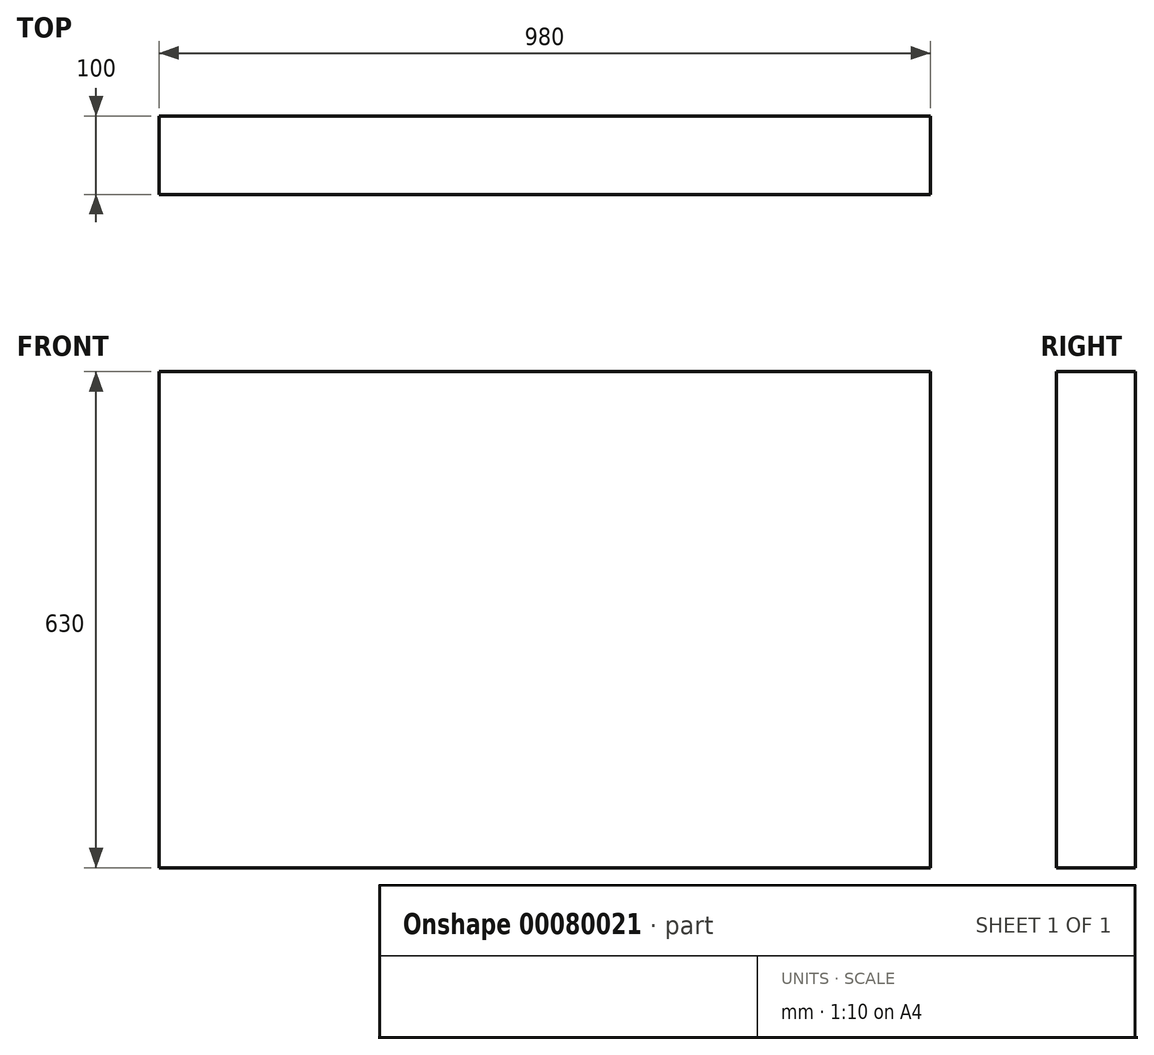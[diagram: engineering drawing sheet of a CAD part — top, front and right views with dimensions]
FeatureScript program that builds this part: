
annotation { "Feature Type Name" : "Feature", "Feature Type Description" : "" }
export const myFeature = defineFeature(function(context is Context, id is Id, definition is map)
    precondition{}
    {
        {
            var Q0;
            Q0=qCreatedBy(makeId("Front.planeOp"),FACE);
            var sketch = newSketch(context, id + "F0", { "sketchPlane" : qUnion([Q0])});
            skLineSegment(sketch, "E0.bottom", {"start": v(0, 0) * mm, "end": v(980, 0) * mm});
            skLineSegment(sketch, "E0.top", {"start": v(0, -630) * mm, "end": v(980, -630) * mm});
            skLineSegment(sketch, "E0.left", {"start": v(0, 0) * mm, "end": v(0, -630) * mm});
            skLineSegment(sketch, "E0.right", {"start": v(980, 0) * mm, "end": v(980, -630) * mm});
            skSolve(sketch);
        }
        {
            var Q0;
            Q0=makeQuery(id+"F0.imprint","IMPRINT",FACE,{"disambiguationData":[TD([[makeQuery(id+"F0.imprint","IMPRINT",EDGE,{"derivedFrom":sQuery(id+"F0.wireOp",EDGE,"E0.bottom")}),-1.0]])]});
            extrude(context, id + "F1", {"entities" : qUnion([Q0]), "depth" : 100 * mm});
        }
    });
